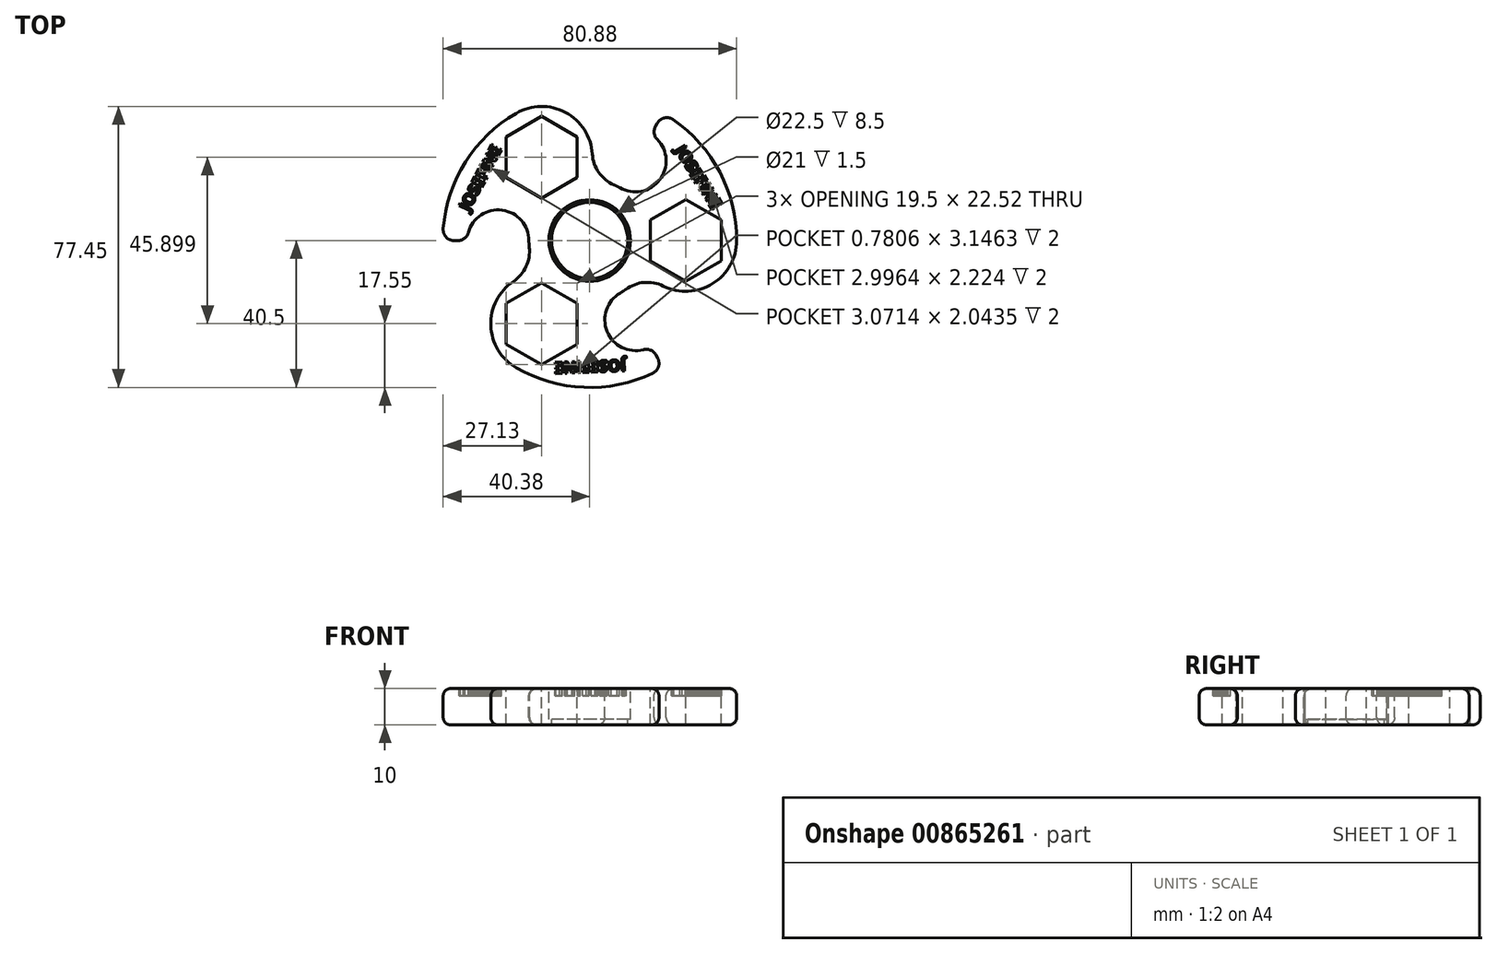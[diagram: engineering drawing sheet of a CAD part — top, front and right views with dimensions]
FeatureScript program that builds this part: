
annotation { "Feature Type Name" : "Feature", "Feature Type Description" : "" }
export const myFeature = defineFeature(function(context is Context, id is Id, definition is map)
    precondition{}
    {
        {
            var Q0;
            Q0=qCreatedBy(makeId("Top.planeOp"),FACE);
            var sketch = newSketch(context, id + "F0", { "sketchPlane" : qUnion([Q0])});
            skCircle(sketch, "E0", {"center": v(0, 0) * mm, "radius": 11.25 * mm});
            skCircle(sketch, "E1.cCircle", {"center": v(26.5, 0) * mm, "radius": 9.75 * mm, "construction": true});
            skLineSegment(sketch, "E1.0", {"start": v(36.25, 5.63) * mm, "end": v(36.25, -5.63) * mm});
            skLineSegment(sketch, "E1.1", {"start": v(36.25, -5.63) * mm, "end": v(26.5, -11.26) * mm});
            skLineSegment(sketch, "E1.2", {"start": v(26.5, -11.26) * mm, "end": v(16.75, -5.63) * mm});
            skLineSegment(sketch, "E1.3", {"start": v(16.75, -5.63) * mm, "end": v(16.75, 5.63) * mm});
            skLineSegment(sketch, "E1.4", {"start": v(16.75, 5.63) * mm, "end": v(26.5, 11.26) * mm});
            skLineSegment(sketch, "E1.5", {"start": v(26.5, 11.26) * mm, "end": v(36.25, 5.63) * mm});
            skPoint(sketch, "E1.0.midPoint", {"position": v(9.75, 0) * mm});
            skLineSegment(sketch, "E2", {"start": v(26.5, 11.26) * mm, "end": v(16.75, 5.63) * mm});
            skLineSegment(sketch, "E3", {"start": v(16.75, 5.63) * mm, "end": v(16.75, -5.63) * mm});
            skLineSegment(sketch, "E4", {"start": v(16.75, -5.63) * mm, "end": v(26.5, -11.26) * mm});
            skLineSegment(sketch, "E5", {"start": v(26.5, -11.26) * mm, "end": v(36.25, -5.63) * mm});
            skLineSegment(sketch, "E6", {"start": v(36.25, -5.63) * mm, "end": v(36.25, 5.63) * mm});
            skLineSegment(sketch, "E7", {"start": v(36.25, 5.63) * mm, "end": v(26.5, 11.26) * mm});
            skArc(sketch, "E8", {"start": v(8.38, 14.5) * mm, "mid": v(7.55, 14.95) * mm, "end": v(6.7, 15.35) * mm});
            skArc(sketch, "E9", {"start": v(20.3, -12.56) * mm, "mid": v(33.9, -11.89) * mm, "end": v(40.5, 0) * mm});
            skArc(sketch, "E10", {"start": v(40.5, 0) * mm, "mid": v(35.85, 18.84) * mm, "end": v(22.97, 33.35) * mm});
            skLineSegment(sketch, "E11", {"start": v(8.32, 14.54) * mm, "end": v(8.32, 14.54) * mm});
            skArc(sketch, "E12", {"start": v(8.32, 14.54) * mm, "mid": v(19.3, 16.7) * mm, "end": v(18.62, 27.87) * mm});
            skLineSegment(sketch, "E13", {"start": v(0, 0) * mm, "end": v(44.66, 0) * mm});
            skLineSegment(sketch, "E14.trimOffspring", {"start": v(18.16, 31.5) * mm, "end": v(18.68, 32.39) * mm});
            skPoint(sketch, "E15.visualSharp", {"position": v(14.85, -7.76) * mm});
            skArc(sketch, "E15.filletArc", {"start": v(20.3, -12.56) * mm, "mid": v(15, -11.56) * mm, "end": v(9.95, -13.48) * mm});
            skPoint(sketch, "E16.visualSharp", {"position": v(20.24, 35.08) * mm});
            skArc(sketch, "E16.filletArc", {"start": v(22.97, 33.35) * mm, "mid": v(20.62, 33.8) * mm, "end": v(18.68, 32.39) * mm});
            skPoint(sketch, "E17.visualSharp", {"position": v(16.85, 29.24) * mm});
            skArc(sketch, "E17.filletArc", {"start": v(18.16, 31.5) * mm, "mid": v(17.78, 29.6) * mm, "end": v(18.62, 27.87) * mm});
            skArc(sketch, "E18.1.0", {"start": v(-16.75, -0.07) * mm, "mid": v(-24.11, 8.38) * mm, "end": v(-33.45, 2.19) * mm});
            skArc(sketch, "E18.1.1", {"start": v(-36.35, -0.02) * mm, "mid": v(-34.53, 0.6) * mm, "end": v(-33.45, 2.19) * mm});
            skLineSegment(sketch, "E18.1.2", {"start": v(-36.35, -0.02) * mm, "end": v(-37.39, -0.02) * mm});
            skArc(sketch, "E18.1.3", {"start": v(-40.37, 3.22) * mm, "mid": v(-39.59, 0.95) * mm, "end": v(-37.39, -0.02) * mm});
            skArc(sketch, "E18.1.4", {"start": v(-20.25, 35.07) * mm, "mid": v(-34.24, 21.63) * mm, "end": v(-40.37, 3.22) * mm});
            skArc(sketch, "E18.1.5", {"start": v(0.72, 23.86) * mm, "mid": v(-6.65, 35.3) * mm, "end": v(-20.25, 35.07) * mm});
            skArc(sketch, "E18.1.6", {"start": v(0.72, 23.86) * mm, "mid": v(2.52, 18.77) * mm, "end": v(6.7, 15.35) * mm});
            skLineSegment(sketch, "E18.1.7", {"start": v(-3.5, 17.32) * mm, "end": v(-3.5, 28.58) * mm});
            skLineSegment(sketch, "E18.1.8", {"start": v(-3.5, 28.58) * mm, "end": v(-13.25, 34.2) * mm});
            skLineSegment(sketch, "E18.1.9", {"start": v(-13.25, 34.2) * mm, "end": v(-23, 28.58) * mm});
            skLineSegment(sketch, "E18.1.10", {"start": v(-23, 28.58) * mm, "end": v(-23, 17.32) * mm});
            skLineSegment(sketch, "E18.1.11", {"start": v(-23, 17.32) * mm, "end": v(-13.25, 11.7) * mm});
            skLineSegment(sketch, "E18.1.12", {"start": v(-13.25, 11.7) * mm, "end": v(-3.5, 17.32) * mm});
            skArc(sketch, "E18.2.0", {"start": v(8.43, -14.47) * mm, "mid": v(4.8, -25.07) * mm, "end": v(14.83, -30.06) * mm});
            skArc(sketch, "E18.2.1", {"start": v(18.2, -31.47) * mm, "mid": v(16.75, -30.2) * mm, "end": v(14.83, -30.06) * mm});
            skLineSegment(sketch, "E18.2.2", {"start": v(18.2, -31.47) * mm, "end": v(18.71, -32.37) * mm});
            skArc(sketch, "E18.2.3", {"start": v(17.4, -36.57) * mm, "mid": v(18.97, -34.76) * mm, "end": v(18.71, -32.37) * mm});
            skArc(sketch, "E18.2.4", {"start": v(-20.25, -35.07) * mm, "mid": v(-1.61, -40.47) * mm, "end": v(17.4, -36.57) * mm});
            skArc(sketch, "E18.2.5", {"start": v(-21.03, -11.3) * mm, "mid": v(-27.24, -23.4) * mm, "end": v(-20.25, -35.07) * mm});
            skArc(sketch, "E18.2.6", {"start": v(-21.03, -11.3) * mm, "mid": v(-17.51, -7.2) * mm, "end": v(-16.64, -1.87) * mm});
            skLineSegment(sketch, "E18.2.7", {"start": v(-13.25, -11.7) * mm, "end": v(-23, -17.32) * mm});
            skLineSegment(sketch, "E18.2.8", {"start": v(-23, -17.32) * mm, "end": v(-23, -28.58) * mm});
            skLineSegment(sketch, "E18.2.9", {"start": v(-23, -28.58) * mm, "end": v(-13.25, -34.2) * mm});
            skLineSegment(sketch, "E18.2.10", {"start": v(-13.25, -34.2) * mm, "end": v(-3.5, -28.58) * mm});
            skLineSegment(sketch, "E18.2.11", {"start": v(-3.5, -28.58) * mm, "end": v(-3.5, -17.32) * mm});
            skLineSegment(sketch, "E18.2.12", {"start": v(-3.5, -17.32) * mm, "end": v(-13.25, -11.7) * mm});
            skArc(sketch, "E19.trimOffspring", {"start": v(-16.75, 0) * mm, "mid": v(-16.72, -0.94) * mm, "end": v(-16.64, -1.87) * mm});
            skArc(sketch, "E20.trimOffspring", {"start": v(8.37, -14.5) * mm, "mid": v(9.17, -14.02) * mm, "end": v(9.95, -13.48) * mm});
            skSolve(sketch);
        }
        {
            var Q0;
            Q0=qCreatedBy(makeId("Top.planeOp"),FACE);
            cPlane(context, id + "F1", {"entities" : qUnion([Q0]), "cplaneType" : CPlaneType.OFFSET, "offset" : 5 * mm, "width" : 150 * mm, "height" : 150 * mm});
        }
        {
            var Q0;
            Q0=qCreatedBy(id+"F1.planeOp",FACE);
            var sketch = newSketch(context, id + "F2", { "sketchPlane" : qUnion([Q0])});
            skText(sketch, "E21", { "text": "JOSEFINE", "fontName": "OpenSans-Bold.ttf"});
            const initialGuessF2  = {"E21": [0.02348, 0.02495, 0.53257, -0.84639, 0.00315]};
            skSetInitialGuess(sketch, initialGuessF2);
            skSolve(sketch);
        }
        {
            var Q0;
            Q0=qCreatedBy(makeId("Top.planeOp"),FACE);
            var sketch = newSketch(context, id + "F3", { "sketchPlane" : qUnion([Q0])});
            skCircle(sketch, "E22", {"center": v(0, 0) * mm, "radius": 11.25 * mm});
            skCircle(sketch, "E23", {"center": v(0, 0) * mm, "radius": 10.5 * mm});
            skSolve(sketch);
        }
        {
            var Q0;
            Q0=makeQuery(id+"F0.imprint","IMPRINT",FACE,{"disambiguationData":[TD([[makeQuery(id+"F0.imprint","IMPRINT",EDGE,{"derivedFrom":sQuery(id+"F0.wireOp",EDGE,"E0")}),-1.0]])]});
            extrude(context, id + "F4", {"entities" : qUnion([Q0]), "depth" : -10 * mm, "offsetDistance" : 25 * mm});
        }
        {
            var Q0;
            Q0=makeQuery(id+"F3.imprint","IMPRINT",FACE,{"disambiguationData":[TD([[makeQuery(id+"F3.imprint","IMPRINT",EDGE,{"derivedFrom":sQuery(id+"F3.wireOp",EDGE,"E22")}),1.0]])]});
            extrude(context, id + "F5", {"entities" : qUnion([Q0]), "depth" : -1 * mm, "offsetDistance" : 25 * mm});
        }
        {
            var Q0;
            Q0=qSketchRegion(id+"F2",true);
            extrude(context, id + "F6", {"entities" : qUnion([Q0]), "depth" : -7 * mm, "offsetDistance" : 25 * mm});
        }
        {
            var Q0;
            Q0=makeQuery(id+"F4.opExtrude","CAP_EDGE",EDGE,{"disambiguationData":[OSD([sQuery(id+"F0.wireOp",EDGE,"E18.1.4")])],"isStart":true});
            var Q1;
            Q1=makeQuery(id+"F4.opExtrude","CAP_EDGE",EDGE,{"disambiguationData":[OSD([sQuery(id+"F0.wireOp",EDGE,"E18.1.5")])],"isStart":true});
            var Q2;
            Q2=makeQuery(id+"F4.opExtrude","CAP_EDGE",EDGE,{"disambiguationData":[OSD([sQuery(id+"F0.wireOp",EDGE,"E12")])],"isStart":true});
            var Q3;
            Q3=makeQuery(id+"F4.opExtrude","CAP_EDGE",EDGE,{"disambiguationData":[OSD([sQuery(id+"F0.wireOp",EDGE,"E18.2.2")])],"isStart":true});
            fillet(context, id + "F7", {"entities" : qUnion([Q0, Q1, Q2, Q3]), "radius" : 2 * mm, "tangentPropagation" : true, "allowEdgeOverflow" : false});
        }
        {
            var Q0;
            Q0=makeQuery(id+"F4.opExtrude","CAP_EDGE",EDGE,{"disambiguationData":[OSD([sQuery(id+"F0.wireOp",EDGE,"E18.2.4")])],"isStart":false});
            var Q1;
            Q1=makeQuery(id+"F4.opExtrude","CAP_EDGE",EDGE,{"disambiguationData":[OSD([sQuery(id+"F0.wireOp",EDGE,"E18.2.3")])],"isStart":false});
            var Q2;
            Q2=makeQuery(id+"F4.opExtrude","CAP_EDGE",EDGE,{"disambiguationData":[OSD([sQuery(id+"F0.wireOp",EDGE,"E9")])],"isStart":false});
            var Q3;
            Q3=makeQuery(id+"F4.opExtrude","CAP_EDGE",EDGE,{"disambiguationData":[OSD([sQuery(id+"F0.wireOp",EDGE,"E18.1.5")])],"isStart":false});
            fillet(context, id + "F8", {"entities" : qUnion([Q0, Q1, Q2, Q3]), "radius" : 2 * mm, "tangentPropagation" : true, "allowEdgeOverflow" : false});
        }
        {
            var Q0;
            Q0=makeQuery(id+"F6.opExtrude","SWEPT_BODY",BODY,{"disambiguationData":[OSD([sQuery(id+"F2.wireOp",EDGE,"E21.sketch_text.stroke-10"),sQuery(id+"F2.wireOp",EDGE,"E21.sketch_text.stroke-11"),sQuery(id+"F2.wireOp",EDGE,"E21.sketch_text.stroke-12"),sQuery(id+"F2.wireOp",EDGE,"E21.sketch_text.stroke-13"),sQuery(id+"F2.wireOp",EDGE,"E21.sketch_text.stroke-14"),sQuery(id+"F2.wireOp",EDGE,"E21.sketch_text.stroke-15"),sQuery(id+"F2.wireOp",EDGE,"E21.sketch_text.stroke-16"),sQuery(id+"F2.wireOp",EDGE,"E21.sketch_text.stroke-17"),sQuery(id+"F2.wireOp",EDGE,"E21.sketch_text.stroke-18"),sQuery(id+"F2.wireOp",EDGE,"E21.sketch_text.stroke-19"),sQuery(id+"F2.wireOp",EDGE,"E21.sketch_text.stroke-20"),sQuery(id+"F2.wireOp",EDGE,"E21.sketch_text.stroke-21"),sQuery(id+"F2.wireOp",EDGE,"E21.sketch_text.stroke-22"),sQuery(id+"F2.wireOp",EDGE,"E21.sketch_text.stroke-23")])]});
            var Q1;
            Q1=makeQuery(id+"F6.opExtrude","SWEPT_BODY",BODY,{"disambiguationData":[OSD([sQuery(id+"F2.wireOp",EDGE,"E21.sketch_text.stroke-0"),sQuery(id+"F2.wireOp",EDGE,"E21.sketch_text.stroke-1"),sQuery(id+"F2.wireOp",EDGE,"E21.sketch_text.stroke-2"),sQuery(id+"F2.wireOp",EDGE,"E21.sketch_text.stroke-3"),sQuery(id+"F2.wireOp",EDGE,"E21.sketch_text.stroke-4"),sQuery(id+"F2.wireOp",EDGE,"E21.sketch_text.stroke-5"),sQuery(id+"F2.wireOp",EDGE,"E21.sketch_text.stroke-6"),sQuery(id+"F2.wireOp",EDGE,"E21.sketch_text.stroke-7"),sQuery(id+"F2.wireOp",EDGE,"E21.sketch_text.stroke-8"),sQuery(id+"F2.wireOp",EDGE,"E21.sketch_text.stroke-9")])]});
            var Q2;
            Q2=makeQuery(id+"F6.opExtrude","SWEPT_BODY",BODY,{"disambiguationData":[OSD([sQuery(id+"F2.wireOp",EDGE,"E21.sketch_text.stroke-24"),sQuery(id+"F2.wireOp",EDGE,"E21.sketch_text.stroke-25"),sQuery(id+"F2.wireOp",EDGE,"E21.sketch_text.stroke-26"),sQuery(id+"F2.wireOp",EDGE,"E21.sketch_text.stroke-27"),sQuery(id+"F2.wireOp",EDGE,"E21.sketch_text.stroke-28"),sQuery(id+"F2.wireOp",EDGE,"E21.sketch_text.stroke-29"),sQuery(id+"F2.wireOp",EDGE,"E21.sketch_text.stroke-30"),sQuery(id+"F2.wireOp",EDGE,"E21.sketch_text.stroke-31"),sQuery(id+"F2.wireOp",EDGE,"E21.sketch_text.stroke-32"),sQuery(id+"F2.wireOp",EDGE,"E21.sketch_text.stroke-33"),sQuery(id+"F2.wireOp",EDGE,"E21.sketch_text.stroke-34"),sQuery(id+"F2.wireOp",EDGE,"E21.sketch_text.stroke-35"),sQuery(id+"F2.wireOp",EDGE,"E21.sketch_text.stroke-36"),sQuery(id+"F2.wireOp",EDGE,"E21.sketch_text.stroke-37"),sQuery(id+"F2.wireOp",EDGE,"E21.sketch_text.stroke-38"),sQuery(id+"F2.wireOp",EDGE,"E21.sketch_text.stroke-39"),sQuery(id+"F2.wireOp",EDGE,"E21.sketch_text.stroke-40"),sQuery(id+"F2.wireOp",EDGE,"E21.sketch_text.stroke-41"),sQuery(id+"F2.wireOp",EDGE,"E21.sketch_text.stroke-42"),sQuery(id+"F2.wireOp",EDGE,"E21.sketch_text.stroke-43"),sQuery(id+"F2.wireOp",EDGE,"E21.sketch_text.stroke-44"),sQuery(id+"F2.wireOp",EDGE,"E21.sketch_text.stroke-45"),sQuery(id+"F2.wireOp",EDGE,"E21.sketch_text.stroke-46"),sQuery(id+"F2.wireOp",EDGE,"E21.sketch_text.stroke-47"),sQuery(id+"F2.wireOp",EDGE,"E21.sketch_text.stroke-48"),sQuery(id+"F2.wireOp",EDGE,"E21.sketch_text.stroke-49"),sQuery(id+"F2.wireOp",EDGE,"E21.sketch_text.stroke-50"),sQuery(id+"F2.wireOp",EDGE,"E21.sketch_text.stroke-51")])]});
            var Q3;
            Q3=makeQuery(id+"F6.opExtrude","SWEPT_BODY",BODY,{"disambiguationData":[OSD([sQuery(id+"F2.wireOp",EDGE,"E21.sketch_text.stroke-52"),sQuery(id+"F2.wireOp",EDGE,"E21.sketch_text.stroke-53"),sQuery(id+"F2.wireOp",EDGE,"E21.sketch_text.stroke-54"),sQuery(id+"F2.wireOp",EDGE,"E21.sketch_text.stroke-55"),sQuery(id+"F2.wireOp",EDGE,"E21.sketch_text.stroke-56"),sQuery(id+"F2.wireOp",EDGE,"E21.sketch_text.stroke-57"),sQuery(id+"F2.wireOp",EDGE,"E21.sketch_text.stroke-58"),sQuery(id+"F2.wireOp",EDGE,"E21.sketch_text.stroke-59"),sQuery(id+"F2.wireOp",EDGE,"E21.sketch_text.stroke-60"),sQuery(id+"F2.wireOp",EDGE,"E21.sketch_text.stroke-61"),sQuery(id+"F2.wireOp",EDGE,"E21.sketch_text.stroke-62"),sQuery(id+"F2.wireOp",EDGE,"E21.sketch_text.stroke-63")])]});
            var Q4;
            Q4=makeQuery(id+"F6.opExtrude","SWEPT_BODY",BODY,{"disambiguationData":[OSD([sQuery(id+"F2.wireOp",EDGE,"E21.sketch_text.stroke-64"),sQuery(id+"F2.wireOp",EDGE,"E21.sketch_text.stroke-65"),sQuery(id+"F2.wireOp",EDGE,"E21.sketch_text.stroke-66"),sQuery(id+"F2.wireOp",EDGE,"E21.sketch_text.stroke-67"),sQuery(id+"F2.wireOp",EDGE,"E21.sketch_text.stroke-68"),sQuery(id+"F2.wireOp",EDGE,"E21.sketch_text.stroke-69"),sQuery(id+"F2.wireOp",EDGE,"E21.sketch_text.stroke-70"),sQuery(id+"F2.wireOp",EDGE,"E21.sketch_text.stroke-71"),sQuery(id+"F2.wireOp",EDGE,"E21.sketch_text.stroke-72"),sQuery(id+"F2.wireOp",EDGE,"E21.sketch_text.stroke-73")])]});
            var Q5;
            Q5=makeQuery(id+"F6.opExtrude","SWEPT_BODY",BODY,{"disambiguationData":[OSD([sQuery(id+"F2.wireOp",EDGE,"E21.sketch_text.stroke-74"),sQuery(id+"F2.wireOp",EDGE,"E21.sketch_text.stroke-75"),sQuery(id+"F2.wireOp",EDGE,"E21.sketch_text.stroke-76"),sQuery(id+"F2.wireOp",EDGE,"E21.sketch_text.stroke-77")])]});
            var Q6;
            Q6=makeQuery(id+"F6.opExtrude","SWEPT_BODY",BODY,{"disambiguationData":[OSD([sQuery(id+"F2.wireOp",EDGE,"E21.sketch_text.stroke-78"),sQuery(id+"F2.wireOp",EDGE,"E21.sketch_text.stroke-79"),sQuery(id+"F2.wireOp",EDGE,"E21.sketch_text.stroke-80"),sQuery(id+"F2.wireOp",EDGE,"E21.sketch_text.stroke-81"),sQuery(id+"F2.wireOp",EDGE,"E21.sketch_text.stroke-82"),sQuery(id+"F2.wireOp",EDGE,"E21.sketch_text.stroke-83"),sQuery(id+"F2.wireOp",EDGE,"E21.sketch_text.stroke-84"),sQuery(id+"F2.wireOp",EDGE,"E21.sketch_text.stroke-85"),sQuery(id+"F2.wireOp",EDGE,"E21.sketch_text.stroke-86"),sQuery(id+"F2.wireOp",EDGE,"E21.sketch_text.stroke-87"),sQuery(id+"F2.wireOp",EDGE,"E21.sketch_text.stroke-88"),sQuery(id+"F2.wireOp",EDGE,"E21.sketch_text.stroke-89"),sQuery(id+"F2.wireOp",EDGE,"E21.sketch_text.stroke-90"),sQuery(id+"F2.wireOp",EDGE,"E21.sketch_text.stroke-91")])]});
            var Q7;
            Q7=makeQuery(id+"F6.opExtrude","SWEPT_BODY",BODY,{"disambiguationData":[OSD([sQuery(id+"F2.wireOp",EDGE,"E21.sketch_text.stroke-92"),sQuery(id+"F2.wireOp",EDGE,"E21.sketch_text.stroke-93"),sQuery(id+"F2.wireOp",EDGE,"E21.sketch_text.stroke-94"),sQuery(id+"F2.wireOp",EDGE,"E21.sketch_text.stroke-95"),sQuery(id+"F2.wireOp",EDGE,"E21.sketch_text.stroke-96"),sQuery(id+"F2.wireOp",EDGE,"E21.sketch_text.stroke-97"),sQuery(id+"F2.wireOp",EDGE,"E21.sketch_text.stroke-98"),sQuery(id+"F2.wireOp",EDGE,"E21.sketch_text.stroke-99"),sQuery(id+"F2.wireOp",EDGE,"E21.sketch_text.stroke-100"),sQuery(id+"F2.wireOp",EDGE,"E21.sketch_text.stroke-101"),sQuery(id+"F2.wireOp",EDGE,"E21.sketch_text.stroke-102"),sQuery(id+"F2.wireOp",EDGE,"E21.sketch_text.stroke-103")])]});
            var Q8;
            Q8=makeQuery(id+"F5.opExtrude","CAP_EDGE",EDGE,{"disambiguationData":[OSD([sQuery(id+"F3.wireOp",EDGE,"E23")])],"isStart":true});
            circularPattern(context, id + "F9", {"operationType" : NewBodyOperationType.REMOVE, "entities" : qUnion([Q0, Q1, Q2, Q3, Q4, Q5, Q6, Q7]), "axis" : qUnion([Q8]), "angle" : 360 * degree, "instanceCount" : 3, "equalSpace" : true, "computeTransformsWithoutBuiltin" : true});
        }
        {
            var Q0;
            Q0=makeQuery(id+"F5.opExtrude","SWEPT_BODY",BODY,{"disambiguationData":[OSD([sQuery(id+"F3.wireOp",EDGE,"E22"),sQuery(id+"F3.wireOp",EDGE,"E23")])]});
            transform(context, id + "F10", {"entities" : qUnion([Q0]), "transformType" : TransformType.TRANSLATION_3D, "dx" : 0 * mm, "dy" : 0 * mm, "dz" : -9 * mm, "makeCopy" : false});
        }
        {
            var Q0;
            Q0=makeQuery(id+"F5.opExtrude","CAP_FACE",FACE,{"disambiguationData":[OSD([sQuery(id+"F3.wireOp",EDGE,"E22"),sQuery(id+"F3.wireOp",EDGE,"E23")])],"isStart":true});
            extrude(context, id + "F11", {"entities" : qUnion([Q0]), "operationType" : NewBodyOperationType.ADD, "depth" : .5 * mm, "offsetDistance" : 25 * mm});
        }
    });
